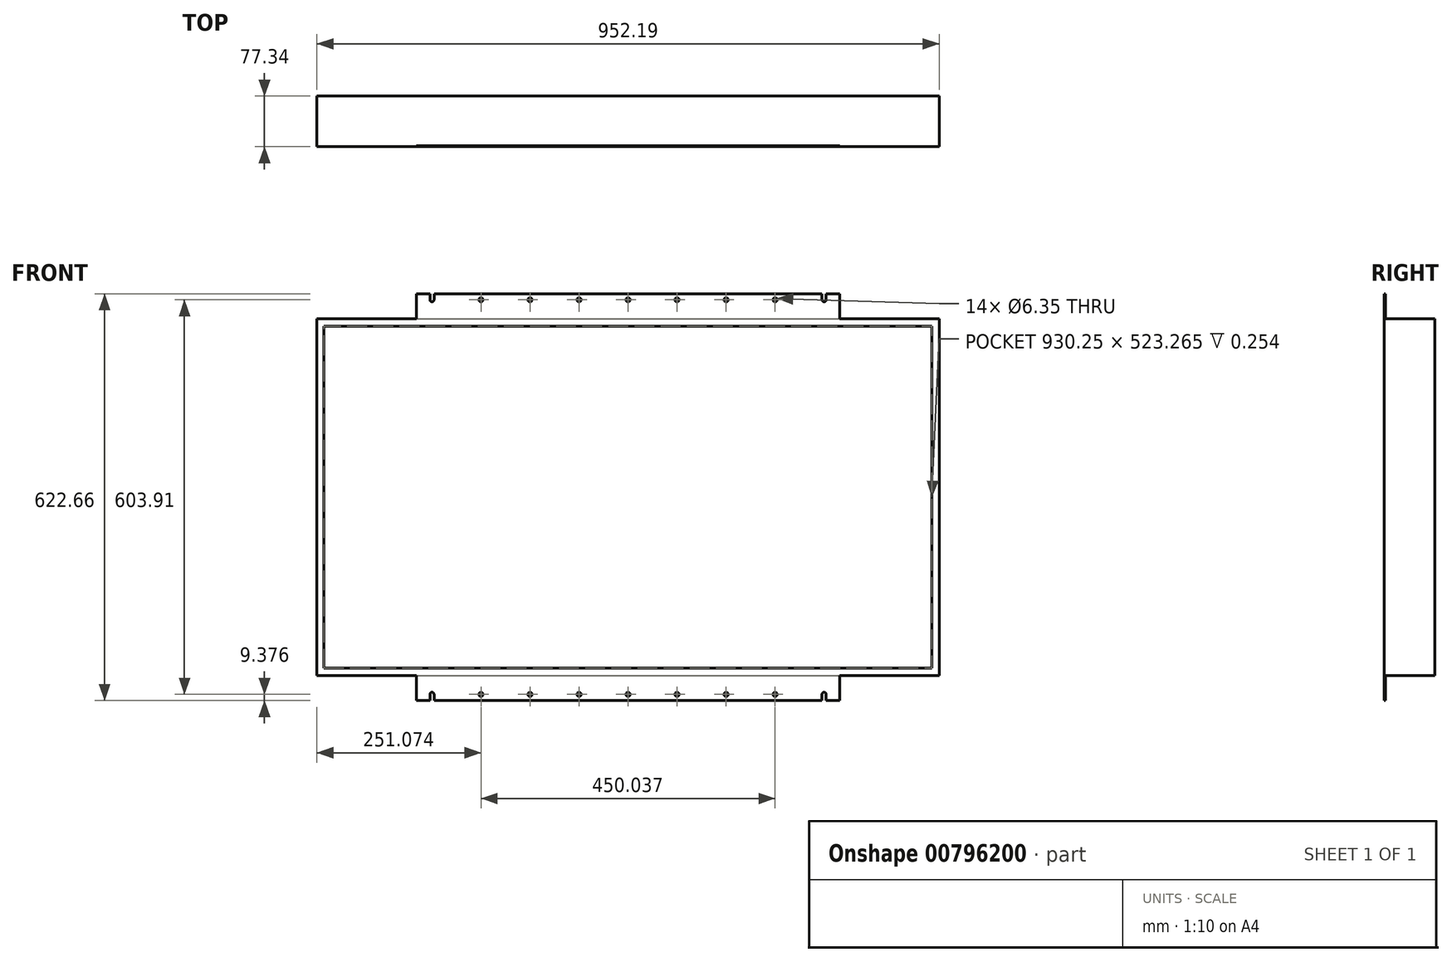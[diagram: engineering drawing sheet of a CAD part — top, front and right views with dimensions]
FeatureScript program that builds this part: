
annotation { "Feature Type Name" : "Feature", "Feature Type Description" : "" }
export const myFeature = defineFeature(function(context is Context, id is Id, definition is map)
    precondition{}
    {
        {
            var Q0;
            Q0=qCreatedBy(makeId("Front.planeOp"),FACE);
            var sketch = newSketch(context, id + "F0", { "sketchPlane" : qUnion([Q0])});
            skLineSegment(sketch, "E0.bottom", {"start": v(-938.54, 519.35) * mm, "end": v(13.65, 519.35) * mm});
            skLineSegment(sketch, "E0.top", {"start": v(-938.54, -26.45) * mm, "end": v(13.65, -26.45) * mm});
            skLineSegment(sketch, "E0.left", {"start": v(-938.54, 519.35) * mm, "end": v(-938.54, -26.45) * mm});
            skLineSegment(sketch, "E0.right", {"start": v(13.65, 519.35) * mm, "end": v(13.65, -26.45) * mm});
            skSolve(sketch);
        }
        {
            var Q0;
            Q0=makeQuery(id+"F0.imprint","IMPRINT",FACE,{"disambiguationData":[TD([[makeQuery(id+"F0.imprint","IMPRINT",EDGE,{"derivedFrom":sQuery(id+"F0.wireOp",EDGE,"E0.bottom")}),-1.0]])]});
            var Q1;
            Q1=sQuery(id+"F0.wireOp",EDGE,"E0.right");
            extrude(context, id + "F1", {"entities" : qUnion([Q0]), "surfaceEntities" : qUnion([Q1]), "depth" : 77.34 * mm, "offsetDistance" : 25.4 * mm});
        }
        {
            var Q0;
            Q0=makeQuery(id+"F1.opExtrude","CAP_FACE",FACE,{"disambiguationData":[OSD([sQuery(id+"F0.wireOp",EDGE,"E0.bottom"),sQuery(id+"F0.wireOp",EDGE,"E0.top"),sQuery(id+"F0.wireOp",EDGE,"E0.left"),sQuery(id+"F0.wireOp",EDGE,"E0.right")])],"isStart":false});
            var sketch = newSketch(context, id + "F2", { "sketchPlane" : qUnion([Q0])});
            skLineSegment(sketch, "E1.bottom", {"start": v(-786.3, 557.78) * mm, "end": v(-138.6, 557.78) * mm});
            skLineSegment(sketch, "E1.top", {"start": v(-786.3, 519.35) * mm, "end": v(-138.6, 519.35) * mm});
            skLineSegment(sketch, "E1.left", {"start": v(-786.3, 557.78) * mm, "end": v(-786.3, 519.35) * mm});
            skLineSegment(sketch, "E1.right", {"start": v(-138.6, 557.78) * mm, "end": v(-138.6, 519.35) * mm});
            skLineSegment(sketch, "E2", {"start": v(-938.54, 246.45) * mm, "end": v(13.65, 246.45) * mm, "construction": true});
            skLineSegment(sketch, "E3", {"start": v(-462.45, 557.78) * mm, "end": v(-462.45, 548.4) * mm});
            skLineSegment(sketch, "E4", {"start": v(-462.45, 548.4) * mm, "end": v(-537.38, 548.4) * mm});
            skLineSegment(sketch, "E5", {"start": v(-462.45, 548.4) * mm, "end": v(-612.46, 548.4) * mm});
            skLineSegment(sketch, "E6", {"start": v(-462.45, 548.4) * mm, "end": v(-687.47, 548.4) * mm});
            skLineSegment(sketch, "E7", {"start": v(-462.45, 548.4) * mm, "end": v(-762.45, 548.4) * mm});
            skCircle(sketch, "E8", {"center": v(-462.45, 548.4) * mm, "radius": 3.18 * mm});
            skCircle(sketch, "E9", {"center": v(-537.38, 548.4) * mm, "radius": 3.18 * mm});
            skCircle(sketch, "E10", {"center": v(-612.46, 548.4) * mm, "radius": 3.18 * mm});
            skCircle(sketch, "E11", {"center": v(-687.47, 548.4) * mm, "radius": 3.18 * mm});
            skArc(sketch, "E12", {"start": v(-765.62, 548.4) * mm, "mid": v(-762.45, 545.23) * mm, "end": v(-759.27, 548.4) * mm});
            skLineSegment(sketch, "E13", {"start": v(-765.62, 548.4) * mm, "end": v(-765.62, 557.78) * mm});
            skLineSegment(sketch, "E14", {"start": v(-759.27, 548.4) * mm, "end": v(-759.27, 557.78) * mm});
            skCircle(sketch, "E15.MirrorC", {"center": v(-981.17, 548.4) * mm, "radius": 3.18 * mm});
            skCircle(sketch, "E16.MirrorC", {"center": v(-387.52, 548.4) * mm, "radius": 3.18 * mm});
            skCircle(sketch, "E17.MirrorC", {"center": v(-312.43, 548.4) * mm, "radius": 3.18 * mm});
            skCircle(sketch, "E18.MirrorC", {"center": v(-237.43, 548.4) * mm, "radius": 3.18 * mm});
            skArc(sketch, "E19.MirrorCS", {"start": v(-159.27, 548.4) * mm, "mid": v(-162.45, 545.23) * mm, "end": v(-165.62, 548.4) * mm});
            skLineSegment(sketch, "E20.MirrorCS", {"start": v(-159.27, 548.4) * mm, "end": v(-159.27, 557.78) * mm});
            skLineSegment(sketch, "E21.MirrorCS", {"start": v(-165.62, 548.4) * mm, "end": v(-165.62, 557.78) * mm});
            skSolve(sketch);
        }
        {
            var Q0;
            {var subQ11=sQuery(id+"F2.wireOp",EDGE,"E1.left");Q0=makeQuery(id+"F2.imprint","IMPRINT",FACE,{"disambiguationData":[TD([[makeQuery(id+"F2.imprint","IMPRINT",EDGE,{"derivedFrom":subQ11}),1.0]])]});}
            var Q1;
            {var subQ8=sQuery(id+"F2.wireOp",EDGE,"E14");Q1=makeQuery(id+"F2.imprint","IMPRINT",FACE,{"disambiguationData":[TD([[makeQuery(id+"F2.imprint","IMPRINT",EDGE,{"derivedFrom":subQ8}),-1.0]])]});}
            extrude(context, id + "F3", {"entities" : qUnion([Q0, Q1]), "oppositeDirection" : true, "depth" : 1.59 * mm, "offsetDistance" : 25.4 * mm});
        }
        {
            var Q0;
            Q0=makeQuery(id+"F1.opExtrude","SWEPT_FACE",FACE,{"disambiguationData":[OSD([sQuery(id+"F0.wireOp",EDGE,"E0.top")])]});
            cPlane(context, id + "F4", {"entities" : qUnion([Q0]), "cplaneType" : CPlaneType.OFFSET, "offset" : 272.9 * mm, "oppositeDirection" : true, "width" : 152.4 * mm, "height" : 152.4 * mm});
        }
        {
            var Q0;
            Q0=makeQuery(id+"F3.opExtrude","SWEPT_BODY",BODY,{"disambiguationData":[OSD([sQuery(id+"F2.wireOp",EDGE,"E1.bottom"),sQuery(id+"F2.wireOp",EDGE,"E1.left"),sQuery(id+"F2.wireOp",EDGE,"E1.right"),sQuery(id+"F2.wireOp",EDGE,"E1.top"),sQuery(id+"F2.wireOp",EDGE,"E8"),sQuery(id+"F2.wireOp",EDGE,"E9"),sQuery(id+"F2.wireOp",EDGE,"E10"),sQuery(id+"F2.wireOp",EDGE,"E11"),sQuery(id+"F2.wireOp",EDGE,"E12"),sQuery(id+"F2.wireOp",EDGE,"E13"),sQuery(id+"F2.wireOp",EDGE,"E14"),sQuery(id+"F2.wireOp",EDGE,"E16.MirrorC"),sQuery(id+"F2.wireOp",EDGE,"E17.MirrorC"),sQuery(id+"F2.wireOp",EDGE,"E18.MirrorC"),sQuery(id+"F2.wireOp",EDGE,"E19.MirrorCS"),sQuery(id+"F2.wireOp",EDGE,"E20.MirrorCS"),sQuery(id+"F2.wireOp",EDGE,"E21.MirrorCS")])]});
            var Q1;
            Q1=qCreatedBy(id+"F4.planeOp",FACE);
            mirror(context, id + "F5", {"operationType" : NewBodyOperationType.ADD, "entities" : qUnion([Q0]), "mirrorPlane" : qUnion([Q1])});
        }
        {
            var Q0;
            Q0=makeQuery(id+"F1.opExtrude","CAP_FACE",FACE,{"disambiguationData":[OSD([sQuery(id+"F0.wireOp",EDGE,"E0.bottom"),sQuery(id+"F0.wireOp",EDGE,"E0.top"),sQuery(id+"F0.wireOp",EDGE,"E0.left"),sQuery(id+"F0.wireOp",EDGE,"E0.right")])],"isStart":false});
            var sketch = newSketch(context, id + "F6", { "sketchPlane" : qUnion([Q0])});
            skLineSegment(sketch, "E22.bottom", {"start": v(-927.57, 508.08) * mm, "end": v(2.68, 508.08) * mm});
            skLineSegment(sketch, "E22.top", {"start": v(-927.57, -15.18) * mm, "end": v(2.68, -15.18) * mm});
            skLineSegment(sketch, "E22.left", {"start": v(-927.57, 508.08) * mm, "end": v(-927.57, -15.18) * mm});
            skLineSegment(sketch, "E22.right", {"start": v(2.68, 508.08) * mm, "end": v(2.68, -15.18) * mm});
            skSolve(sketch);
        }
        {
            var Q0;
            Q0=makeQuery(id+"F6.imprint","IMPRINT",FACE,{"disambiguationData":[TD([[makeQuery(id+"F6.imprint","IMPRINT",EDGE,{"derivedFrom":sQuery(id+"F6.wireOp",EDGE,"E22.bottom")}),-1.0]])]});
            extrude(context, id + "F7", {"entities" : qUnion([Q0]), "operationType" : NewBodyOperationType.REMOVE, "oppositeDirection" : true, "depth" : 0.25 * mm, "offsetDistance" : 25.4 * mm});
        }
    });
